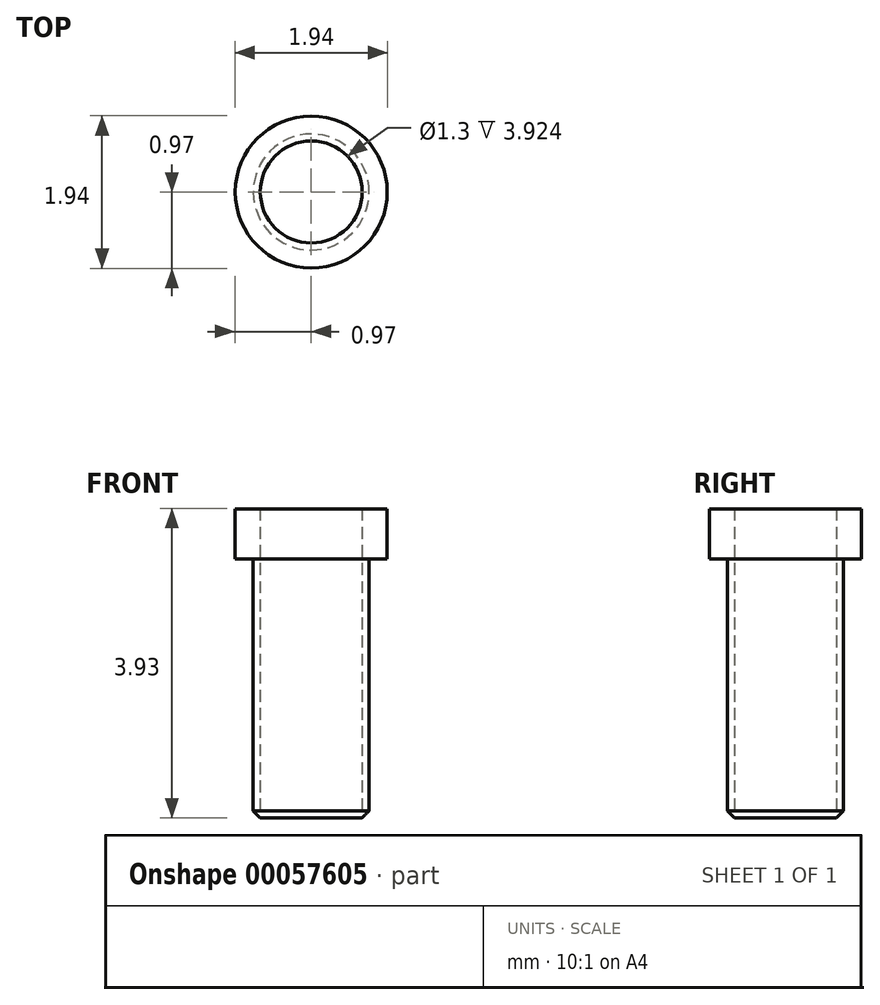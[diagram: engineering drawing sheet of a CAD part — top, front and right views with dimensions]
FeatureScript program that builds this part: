
annotation { "Feature Type Name" : "Feature", "Feature Type Description" : "" }
export const myFeature = defineFeature(function(context is Context, id is Id, definition is map)
    precondition{}
    {
        {
            var Q0;
            Q0=qCreatedBy(makeId("Top.planeOp"),FACE);
            var sketch = newSketch(context, id + "F0", { "sketchPlane" : qUnion([Q0])});
            skCircle(sketch, "E0", {"center": v(0, 0) * mm, "radius": 0.97 * mm});
            skCircle(sketch, "E1", {"center": v(0, 0) * mm, "radius": 0.74 * mm});
            skCircle(sketch, "E2", {"center": v(0, 0) * mm, "radius": 0.65 * mm});
            skSolve(sketch);
        }
        {
            var Q0;
            Q0=makeQuery(id+"F0.imprint","IMPRINT",FACE,{"disambiguationData":[TD([[makeQuery(id+"F0.imprint","IMPRINT",EDGE,{"derivedFrom":sQuery(id+"F0.wireOp",EDGE,"E0")}),1.0]])]});
            var Q1;
            Q1=makeQuery(id+"F0.imprint","IMPRINT",FACE,{"disambiguationData":[TD([[makeQuery(id+"F0.imprint","IMPRINT",EDGE,{"derivedFrom":sQuery(id+"F0.wireOp",EDGE,"E1")}),1.0]])]});
            extrude(context, id + "F1", {"entities" : qUnion([Q0, Q1]), "depth" : 0.64 * mm});
        }
        {
            var Q0;
            Q0=makeQuery(id+"F0.imprint","IMPRINT",FACE,{"disambiguationData":[TD([[makeQuery(id+"F0.imprint","IMPRINT",EDGE,{"derivedFrom":sQuery(id+"F0.wireOp",EDGE,"E1")}),1.0]])]});
            extrude(context, id + "F2", {"entities" : qUnion([Q0]), "operationType" : NewBodyOperationType.ADD, "oppositeDirection" : true, "depth" : 3.3 * mm});
        }
        {
            var Q0;
            Q0=makeQuery(id+"F2.opExtrude","CAP_EDGE",EDGE,{"disambiguationData":[OSD([sQuery(id+"F0.wireOp",EDGE,"E1")])],"isStart":false});
            chamfer(context, id + "F3", {"entities" : qUnion([Q0]), "width" : 0.1 * mm, "tangentPropagation" : true});
        }
    });
